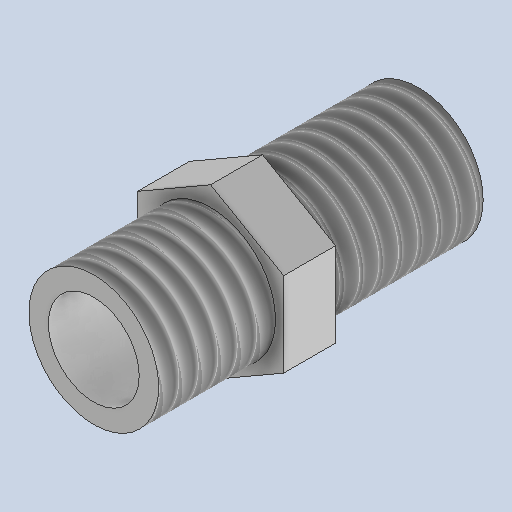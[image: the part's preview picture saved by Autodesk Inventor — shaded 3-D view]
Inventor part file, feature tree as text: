
AUTODESK INVENTOR PART (.ipt)
format: ipt  version: 2025.1 (Build 291241000, 241)  size: 183,296 bytes
history: native  units: mm
features: sketch x4, other x3
ambient origin geometry x8: Origin, YZ Plane, XZ Plane, XY Plane, X Axis, Y Axis, Z Axis, Center Point
bodies: Volumenkörper1 (feature_tree)
feature tree (7):
  other  "1154.ipt"
  other  "Volumenkörper1::1154.ipt"
  other  "TaggingFeature1"
  sketch  "Skizze1"  dims[d0=10.0mm]
  sketch  "Skizze2"
  sketch  "Skizze3"
  sketch  "Skizze4"
